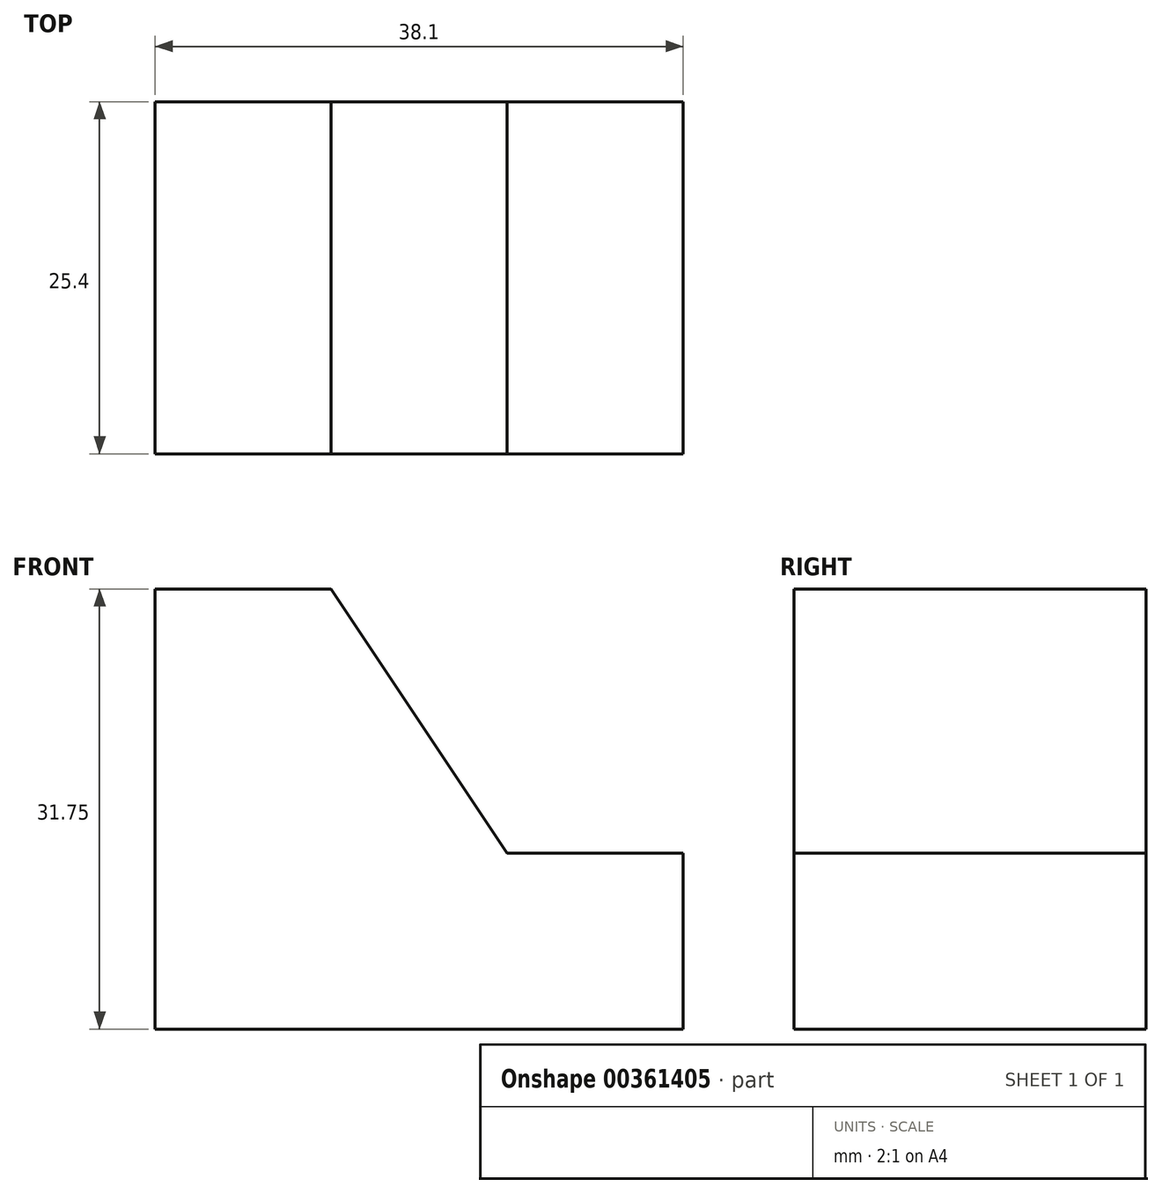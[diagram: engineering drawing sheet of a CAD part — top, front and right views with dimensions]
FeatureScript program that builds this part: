
annotation { "Feature Type Name" : "Feature", "Feature Type Description" : "" }
export const myFeature = defineFeature(function(context is Context, id is Id, definition is map)
    precondition{}
    {
        {
            var Q0;
            Q0=qCreatedBy(makeId("Front.planeOp"),FACE);
            var sketch = newSketch(context, id + "F0", { "sketchPlane" : qUnion([Q0])});
            skLineSegment(sketch, "E0", {"start": v(0, 0) * mm, "end": v(0, 31.75) * mm});
            skLineSegment(sketch, "E1", {"start": v(0, 31.75) * mm, "end": v(12.7, 31.75) * mm});
            skLineSegment(sketch, "E2", {"start": v(12.7, 31.75) * mm, "end": v(25.4, 12.7) * mm});
            skLineSegment(sketch, "E3", {"start": v(25.4, 12.7) * mm, "end": v(38.1, 12.7) * mm});
            skLineSegment(sketch, "E4", {"start": v(38.1, 12.7) * mm, "end": v(38.1, 0) * mm});
            skLineSegment(sketch, "E5", {"start": v(38.1, 0) * mm, "end": v(0, 0) * mm});
            skSolve(sketch);
        }
        {
            var Q0;
            Q0 = qSketchRegion(id + "F0", true);
            extrude(context, id + "F1", {"entities" : qUnion([Q0]), "oppositeDirection" : true, "depth" : 25.4 * mm});
        }
    });
